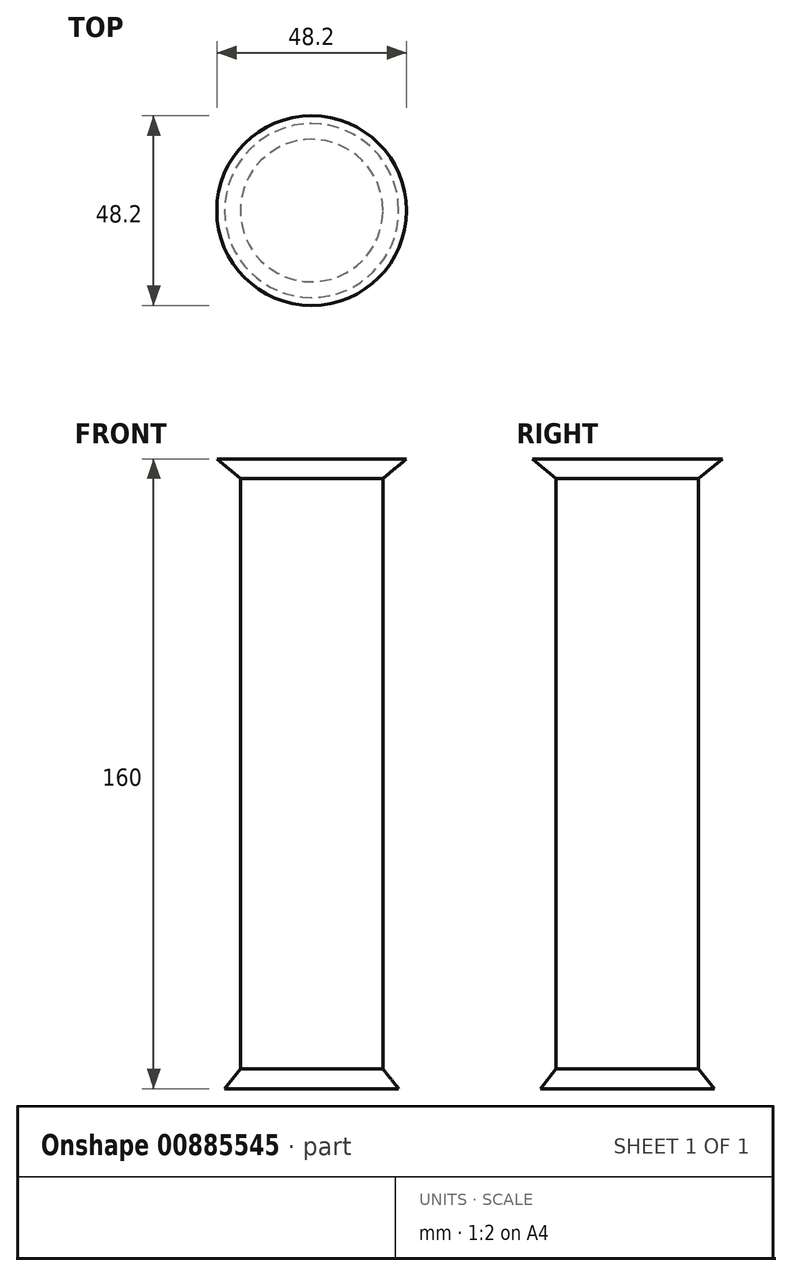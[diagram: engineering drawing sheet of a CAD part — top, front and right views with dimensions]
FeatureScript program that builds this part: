
annotation { "Feature Type Name" : "Feature", "Feature Type Description" : "" }
export const myFeature = defineFeature(function(context is Context, id is Id, definition is map)
    precondition{}
    {
        {
            var Q0;
            Q0=qCreatedBy(makeId("Top.planeOp"),FACE);
            var sketch = newSketch(context, id + "F0", { "sketchPlane" : qUnion([Q0])});
            skCircle(sketch, "E0", {"center": v(0, 0) * mm, "radius": 22.1 * mm});
            skSolve(sketch);
        }
        {
            var Q0;
            Q0=makeQuery(id+"F0.imprint","IMPRINT",FACE,{"disambiguationData":[TD([[makeQuery(id+"F0.imprint","IMPRINT",EDGE,{"derivedFrom":sQuery(id+"F0.wireOp",EDGE,"E0")}),1.0]])]});
            cPlane(context, id + "F1", {"entities" : qUnion([Q0]), "cplaneType" : CPlaneType.OFFSET, "offset" : 5 * mm, "width" : 150 * mm, "height" : 150 * mm});
        }
        {
            var Q0;
            Q0=qCreatedBy(id+"F1.planeOp",FACE);
            var sketch = newSketch(context, id + "F2", { "sketchPlane" : qUnion([Q0])});
            skCircle(sketch, "E1", {"center": v(0, 0) * mm, "radius": 18.1 * mm});
            skSolve(sketch);
        }
        {
            var Q0;
            Q0=makeQuery(id+"F2.imprint","IMPRINT",FACE,{"disambiguationData":[TD([[makeQuery(id+"F2.imprint","IMPRINT",EDGE,{"derivedFrom":sQuery(id+"F2.wireOp",EDGE,"E1")}),1.0]])]});
            cPlane(context, id + "F3", {"entities" : qUnion([Q0]), "cplaneType" : CPlaneType.OFFSET, "offset" : 150 * mm, "width" : 150 * mm, "height" : 150 * mm});
        }
        {
            var Q0;
            Q0=qCreatedBy(id+"F3.planeOp",FACE);
            var sketch = newSketch(context, id + "F4", { "sketchPlane" : qUnion([Q0])});
            skCircle(sketch, "E2.0", {"center": v(0, 0) * mm, "radius": 18.1 * mm});
            skSolve(sketch);
        }
        {
            var Q0;
            Q0=makeQuery(id+"F4.imprint","IMPRINT",FACE,{"disambiguationData":[TD([[makeQuery(id+"F4.imprint","IMPRINT",EDGE,{"derivedFrom":sQuery(id+"F4.wireOp",EDGE,"E2.0")}),1.0]])]});
            cPlane(context, id + "F5", {"entities" : qUnion([Q0]), "cplaneType" : CPlaneType.OFFSET, "offset" : 5 * mm, "width" : 150 * mm, "height" : 150 * mm});
        }
        {
            var Q0;
            Q0=qCreatedBy(id+"F5.planeOp",FACE);
            var sketch = newSketch(context, id + "F6", { "sketchPlane" : qUnion([Q0])});
            skCircle(sketch, "E3.0", {"center": v(0, 0) * mm, "radius": 24.1 * mm});
            skSolve(sketch);
        }
        {
            var Q0;
            Q0=makeQuery(id+"F0.imprint","IMPRINT",FACE,{"disambiguationData":[TD([[makeQuery(id+"F0.imprint","IMPRINT",EDGE,{"derivedFrom":sQuery(id+"F0.wireOp",EDGE,"E0")}),1.0]])]});
            var Q1;
            Q1=makeQuery(id+"F2.imprint","IMPRINT",FACE,{"disambiguationData":[TD([[makeQuery(id+"F2.imprint","IMPRINT",EDGE,{"derivedFrom":sQuery(id+"F2.wireOp",EDGE,"E1")}),1.0]])]});
            loft(context, id + "F7", {"sheetProfilesArray" : [{ "sheetProfileEntities" : qUnion([Q0]) }, { "sheetProfileEntities" : qUnion([Q1]) }]});
        }
        {
            var Q1;
            Q1=makeQuery(id+"F7.opLoft","CAP_FACE",FACE,{"disambiguationData":[OSD([makeQuery(id+"F2.imprint","IMPRINT",FACE,{"disambiguationData":[TD([[makeQuery(id+"F2.imprint","IMPRINT",EDGE,{"derivedFrom":sQuery(id+"F2.wireOp",EDGE,"E1")}),1.0]])]})])],"isStart":true});
            var Q2;
            Q2=makeQuery(id+"F4.imprint","IMPRINT",FACE,{"disambiguationData":[TD([[makeQuery(id+"F4.imprint","IMPRINT",EDGE,{"derivedFrom":sQuery(id+"F4.wireOp",EDGE,"E2.0")}),1.0]])]});
            loft(context, id + "F8", {"operationType" : NewBodyOperationType.ADD, "sheetProfilesArray" : [{ "sheetProfileEntities" : qUnion([Q1]) }, { "sheetProfileEntities" : qUnion([Q2]) }]});
        }
        {
            var Q1;
            Q1=makeQuery(id+"F8.opLoft","CAP_FACE",FACE,{"disambiguationData":[OSD([makeQuery(id+"F4.imprint","IMPRINT",FACE,{"disambiguationData":[TD([[makeQuery(id+"F4.imprint","IMPRINT",EDGE,{"derivedFrom":sQuery(id+"F4.wireOp",EDGE,"E2.0")}),1.0]])]})])],"isStart":true});
            var Q2;
            Q2=makeQuery(id+"F6.imprint","IMPRINT",FACE,{"disambiguationData":[TD([[makeQuery(id+"F6.imprint","IMPRINT",EDGE,{"derivedFrom":sQuery(id+"F6.wireOp",EDGE,"E3.0")}),1.0]])]});
            loft(context, id + "F9", {"operationType" : NewBodyOperationType.ADD, "sheetProfilesArray" : [{ "sheetProfileEntities" : qUnion([Q1]) }, { "sheetProfileEntities" : qUnion([Q2]) }]});
        }
    });
